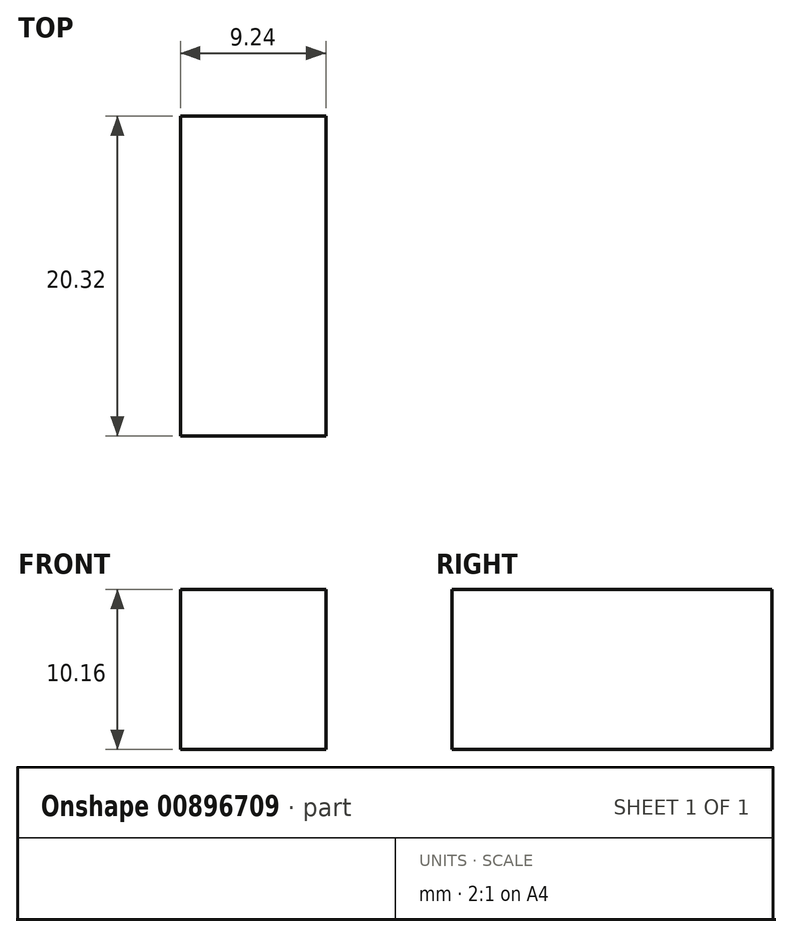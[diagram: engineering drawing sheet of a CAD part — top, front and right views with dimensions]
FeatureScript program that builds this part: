
annotation { "Feature Type Name" : "Feature", "Feature Type Description" : "" }
export const myFeature = defineFeature(function(context is Context, id is Id, definition is map)
    precondition{}
    {
        {
            var Q0;
            Q0=qCreatedBy(makeId("Top.planeOp"),FACE);
            var sketch = newSketch(context, id + "F0", { "sketchPlane" : qUnion([Q0])});
            skLineSegment(sketch, "E0.bottom", {"start": v(-4.62, 10.16) * mm, "end": v(4.62, 10.16) * mm});
            skLineSegment(sketch, "E0.top", {"start": v(-4.62, -10.16) * mm, "end": v(4.62, -10.16) * mm});
            skLineSegment(sketch, "E0.left", {"start": v(-4.62, 10.16) * mm, "end": v(-4.62, -10.16) * mm});
            skLineSegment(sketch, "E0.right", {"start": v(4.62, 10.16) * mm, "end": v(4.62, -10.16) * mm});
            skPoint(sketch, "E0.middle", {"position": v(0, 0) * mm});
            skSolve(sketch);
        }
        {
            var Q0;
            Q0=makeQuery(id+"F0.imprint","IMPRINT",FACE,{"disambiguationData":[TD([[makeQuery(id+"F0.imprint","IMPRINT",EDGE,{"derivedFrom":sQuery(id+"F0.wireOp",EDGE,"E0.bottom")}),-1.0]])]});
            extrude(context, id + "F1", {"entities" : qUnion([Q0]), "depth" : 10.16 * mm, "offsetDistance" : 25.4 * mm});
        }
    });
